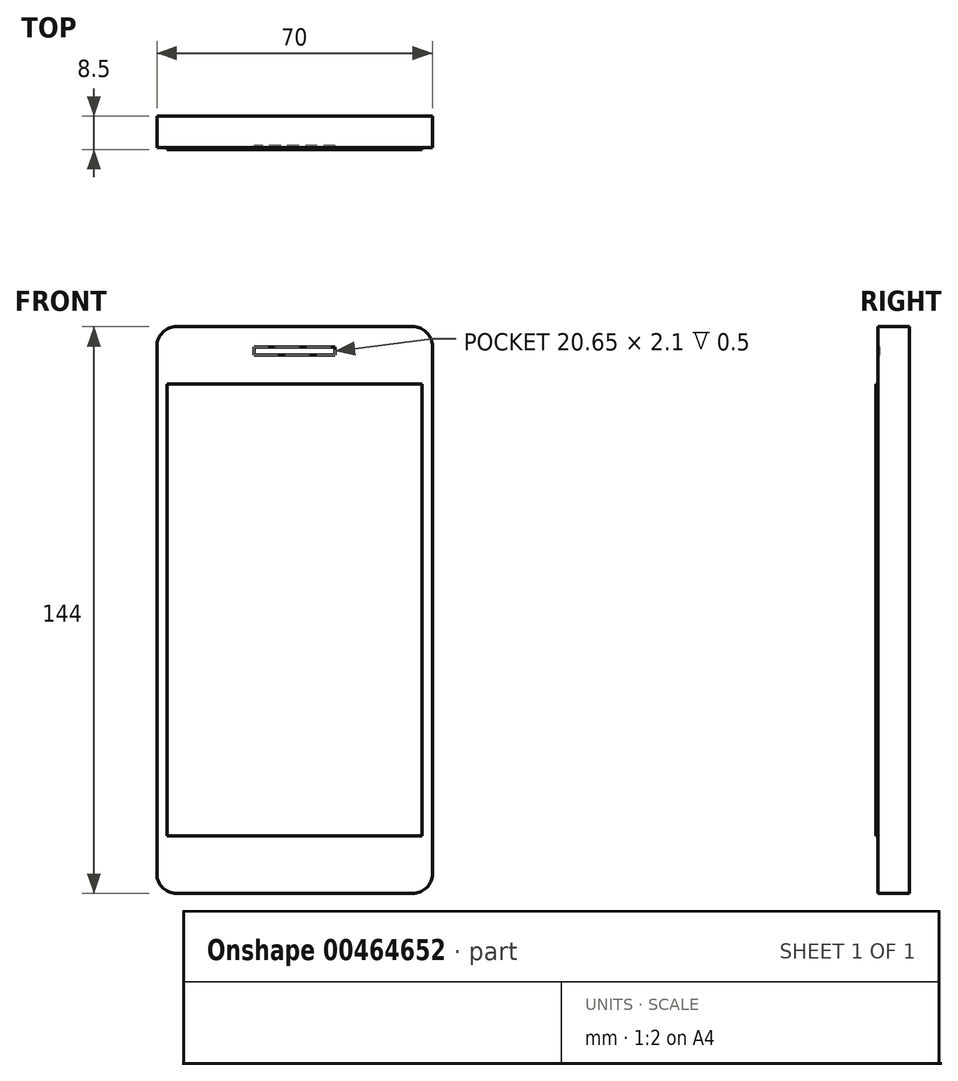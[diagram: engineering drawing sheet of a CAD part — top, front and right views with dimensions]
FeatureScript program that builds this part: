
annotation { "Feature Type Name" : "Feature", "Feature Type Description" : "" }
export const myFeature = defineFeature(function(context is Context, id is Id, definition is map)
    precondition{}
    {
        {
            var Q0;
            Q0=qCreatedBy(makeId("Front.planeOp"),FACE);
            var sketch = newSketch(context, id + "F0", { "sketchPlane" : qUnion([Q0])});
            skLineSegment(sketch, "E0.bottom", {"start": v(-35, 72) * mm, "end": v(35, 72) * mm});
            skLineSegment(sketch, "E0.top", {"start": v(-35, -72) * mm, "end": v(35, -72) * mm});
            skLineSegment(sketch, "E0.left", {"start": v(-35, 72) * mm, "end": v(-35, -72) * mm});
            skLineSegment(sketch, "E0.right", {"start": v(35, 72) * mm, "end": v(35, -72) * mm});
            skPoint(sketch, "E0.middle", {"position": v(0, 0) * mm});
            skSolve(sketch);
        }
        {
            var Q0;
            Q0 = qSketchRegion(id + "F0", true);
            extrude(context, id + "F1", {"entities" : qUnion([Q0]), "depth" : 8 * mm});
        }
        {
            var Q0;
            Q0=makeQuery(id+"F1.opExtrude","SWEPT_EDGE",EDGE,{"disambiguationData":[OSD([sQuery(id+"F0.wireOp",EDGE,"E0.bottom"),sQuery(id+"F0.wireOp",EDGE,"E0.left")])]});
            var Q1;
            Q1=makeQuery(id+"F1.opExtrude","SWEPT_EDGE",EDGE,{"disambiguationData":[OSD([sQuery(id+"F0.wireOp",EDGE,"E0.bottom"),sQuery(id+"F0.wireOp",EDGE,"E0.right")])]});
            var Q2;
            Q2=makeQuery(id+"F1.opExtrude","SWEPT_EDGE",EDGE,{"disambiguationData":[OSD([sQuery(id+"F0.wireOp",EDGE,"E0.top"),sQuery(id+"F0.wireOp",EDGE,"E0.right")])]});
            var Q3;
            Q3=makeQuery(id+"F1.opExtrude","SWEPT_EDGE",EDGE,{"disambiguationData":[OSD([sQuery(id+"F0.wireOp",EDGE,"E0.top"),sQuery(id+"F0.wireOp",EDGE,"E0.left")])]});
            fillet(context, id + "F2", {"entities" : qUnion([Q0, Q1, Q2, Q3]), "radius" : 5 * mm, "tangentPropagation" : true, "allowEdgeOverflow" : false});
        }
        {
            var Q0;
            Q0=makeQuery(id+"F1.opExtrude","CAP_FACE",FACE,{"disambiguationData":[OSD([sQuery(id+"F0.wireOp",EDGE,"E0.bottom"),sQuery(id+"F0.wireOp",EDGE,"E0.top"),sQuery(id+"F0.wireOp",EDGE,"E0.left"),sQuery(id+"F0.wireOp",EDGE,"E0.right")])],"isStart":false});
            var sketch = newSketch(context, id + "F3", { "sketchPlane" : qUnion([Q0])});
            skLineSegment(sketch, "E1.bottom", {"start": v(32.38, 57.4) * mm, "end": v(-32.38, 57.4) * mm});
            skLineSegment(sketch, "E1.top", {"start": v(32.38, -57.4) * mm, "end": v(-32.38, -57.4) * mm});
            skLineSegment(sketch, "E1.left", {"start": v(32.38, 57.4) * mm, "end": v(32.38, -57.4) * mm});
            skLineSegment(sketch, "E1.right", {"start": v(-32.38, 57.4) * mm, "end": v(-32.38, -57.4) * mm});
            skPoint(sketch, "E1.middle", {"position": v(0, 0) * mm});
            skLineSegment(sketch, "E2.bottom", {"start": v(10.33, 64.75) * mm, "end": v(-10.33, 64.75) * mm});
            skLineSegment(sketch, "E2.top", {"start": v(10.33, 66.85) * mm, "end": v(-10.33, 66.85) * mm});
            skLineSegment(sketch, "E2.left", {"start": v(10.33, 64.75) * mm, "end": v(10.33, 66.85) * mm});
            skLineSegment(sketch, "E2.right", {"start": v(-10.33, 64.75) * mm, "end": v(-10.33, 66.85) * mm});
            skPoint(sketch, "E2.middle", {"position": v(0, 65.8) * mm});
            skSolve(sketch);
        }
        {
            var Q0;
            Q0=makeQuery(id+"F3.imprint","IMPRINT",FACE,{"disambiguationData":[TD([[makeQuery(id+"F3.imprint","IMPRINT",EDGE,{"derivedFrom":sQuery(id+"F3.wireOp",EDGE,"E1.bottom")}),1.0]])]});
            extrude(context, id + "F4", {"entities" : qUnion([Q0]), "depth" : .5 * mm});
        }
        {
            var Q0;
            Q0=makeQuery(id+"F3.imprint","IMPRINT",FACE,{"disambiguationData":[TD([[makeQuery(id+"F3.imprint","IMPRINT",EDGE,{"derivedFrom":sQuery(id+"F3.wireOp",EDGE,"E2.bottom")}),-1.0]])]});
            extrude(context, id + "F5", {"entities" : qUnion([Q0]), "operationType" : NewBodyOperationType.REMOVE, "oppositeDirection" : true, "depth" : .5 * mm});
        }
    });
